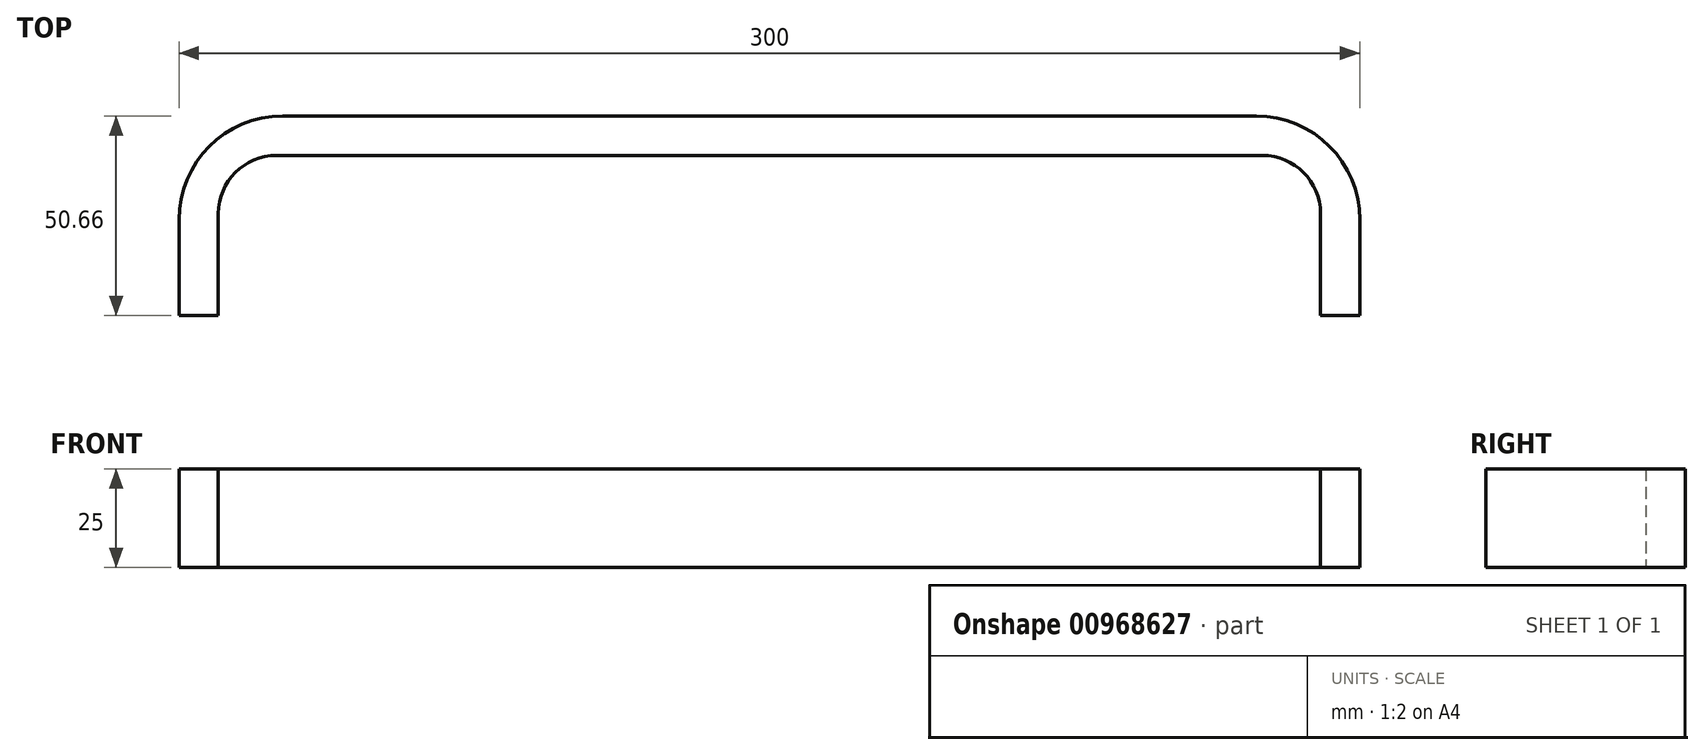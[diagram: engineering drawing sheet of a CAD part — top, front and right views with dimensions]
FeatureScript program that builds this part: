
annotation { "Feature Type Name" : "Feature", "Feature Type Description" : "" }
export const myFeature = defineFeature(function(context is Context, id is Id, definition is map)
    precondition{}
    {
        {
            var Q0;
            Q0=qCreatedBy(makeId("Top.planeOp"),FACE);
            var sketch = newSketch(context, id + "F0", { "sketchPlane" : qUnion([Q0])});
            skLineSegment(sketch, "E0", {"start": v(-151.54, 13.36) * mm, "end": v(148.46, 13.36) * mm});
            skLineSegment(sketch, "E1", {"start": v(-151.54, 13.36) * mm, "end": v(-151.54, -37.3) * mm});
            skLineSegment(sketch, "E2", {"start": v(148.46, 13.36) * mm, "end": v(148.46, -37.3) * mm});
            skLineSegment(sketch, "E3.0", {"start": v(138.46, 3.36) * mm, "end": v(138.46, -37.3) * mm});
            skLineSegment(sketch, "E3.1", {"start": v(-141.54, 3.36) * mm, "end": v(138.46, 3.36) * mm});
            skLineSegment(sketch, "E3.2", {"start": v(-141.54, 3.36) * mm, "end": v(-141.54, -37.3) * mm});
            skLineSegment(sketch, "E4", {"start": v(-151.54, -37.3) * mm, "end": v(-141.54, -37.3) * mm});
            skLineSegment(sketch, "E5", {"start": v(138.46, -37.3) * mm, "end": v(148.46, -37.3) * mm});
            skSolve(sketch);
        }
        {
            var Q0;
            Q0=makeQuery(id+"F0.imprint","IMPRINT",FACE,{"disambiguationData":[TD([[makeQuery(id+"F0.imprint","IMPRINT",EDGE,{"derivedFrom":sQuery(id+"F0.wireOp",EDGE,"E0")}),-1.0]])]});
            extrude(context, id + "F1", {"entities" : qUnion([Q0]), "depth" : 25 * mm, "offsetDistance" : 25 * mm});
        }
        {
            var Q0;
            Q0=makeQuery(id+"F1.opExtrude","SWEPT_EDGE",EDGE,{"disambiguationData":[OSD([sQuery(id+"F0.wireOp",EDGE,"E3.1"),sQuery(id+"F0.wireOp",EDGE,"E3.2")])]});
            var Q1;
            Q1=makeQuery(id+"F1.opExtrude","SWEPT_EDGE",EDGE,{"disambiguationData":[OSD([sQuery(id+"F0.wireOp",EDGE,"E3.0"),sQuery(id+"F0.wireOp",EDGE,"E3.1")])]});
            fillet(context, id + "F2", {"entities" : qUnion([Q0, Q1]), "radius" : 14.73 * mm, "tangentPropagation" : true, "allowEdgeOverflow" : false});
        }
        {
            var Q0;
            Q0=makeQuery(id+"F1.opExtrude","SWEPT_EDGE",EDGE,{"disambiguationData":[OSD([sQuery(id+"F0.wireOp",EDGE,"E0"),sQuery(id+"F0.wireOp",EDGE,"E1")])]});
            var Q1;
            Q1=makeQuery(id+"F1.opExtrude","SWEPT_EDGE",EDGE,{"disambiguationData":[OSD([sQuery(id+"F0.wireOp",EDGE,"E0"),sQuery(id+"F0.wireOp",EDGE,"E2")])]});
            fillet(context, id + "F3", {"entities" : qUnion([Q0, Q1]), "radius" : 26.3 * mm, "tangentPropagation" : true, "allowEdgeOverflow" : false});
        }
    });
